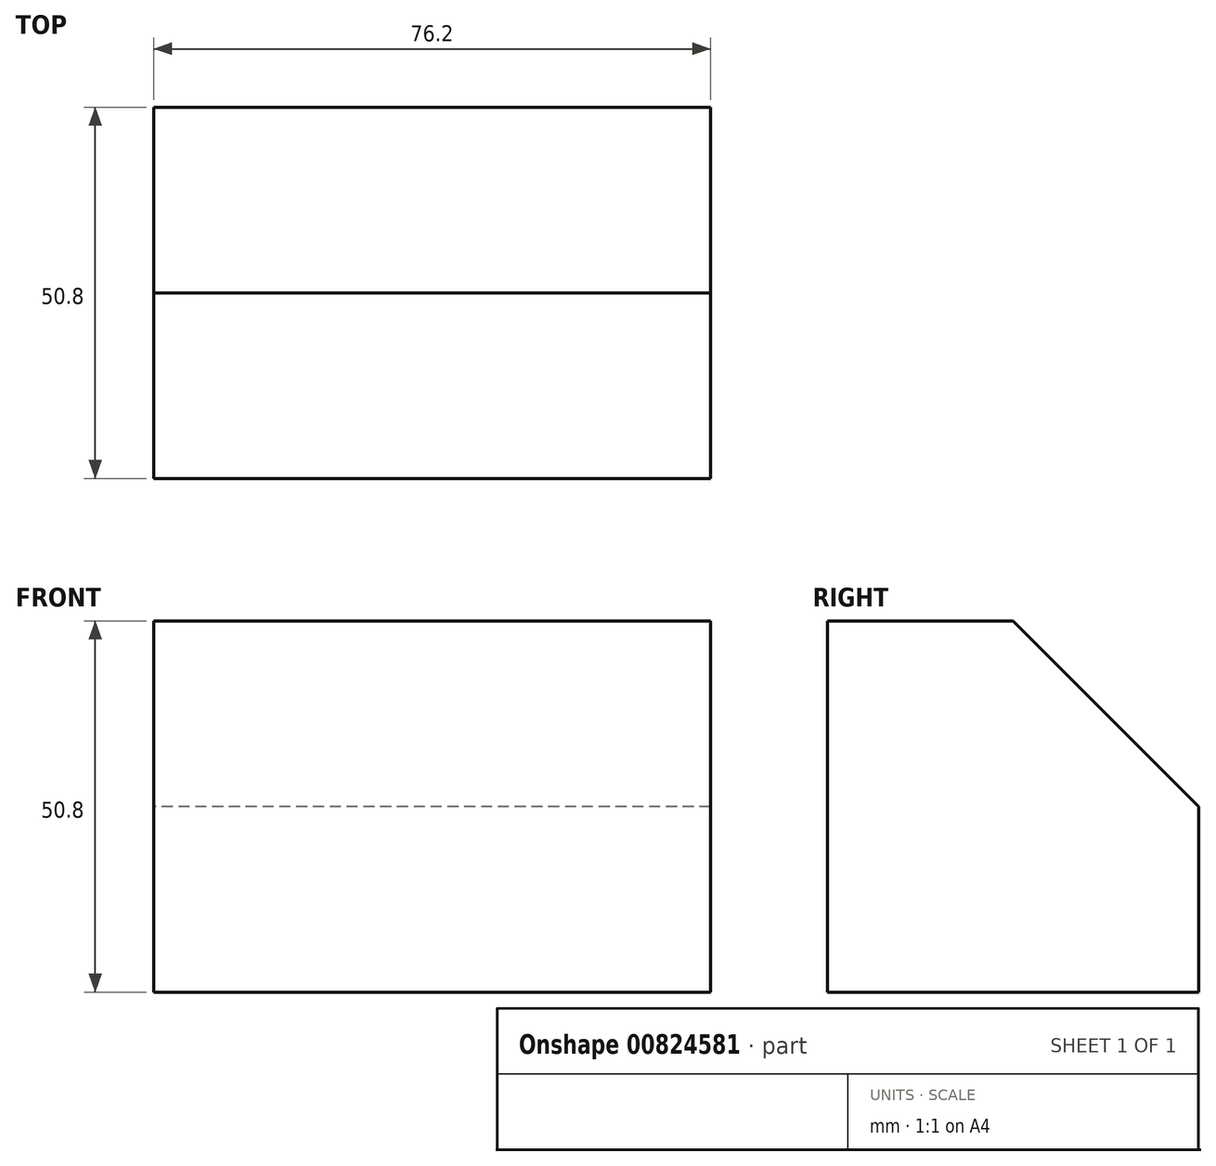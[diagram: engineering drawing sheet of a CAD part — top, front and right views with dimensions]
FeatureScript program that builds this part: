
annotation { "Feature Type Name" : "Feature", "Feature Type Description" : "" }
export const myFeature = defineFeature(function(context is Context, id is Id, definition is map)
    precondition{}
    {
        {
            var Q0;
            Q0=qCreatedBy(makeId("Front.planeOp"),FACE);
            var sketch = newSketch(context, id + "F0", { "sketchPlane" : qUnion([Q0])});
            skLineSegment(sketch, "E0", {"start": v(0, 0) * mm, "end": v(76.2, 0) * mm});
            skLineSegment(sketch, "E1", {"start": v(76.2, 0) * mm, "end": v(76.2, 50.8) * mm});
            skLineSegment(sketch, "E2", {"start": v(76.2, 50.8) * mm, "end": v(0, 50.8) * mm});
            skLineSegment(sketch, "E3", {"start": v(0, 50.8) * mm, "end": v(0, 0) * mm});
            skSolve(sketch);
        }
        {
            var Q0;
            Q0 = qSketchRegion(id + "F0", true);
            extrude(context, id + "F1", {"entities" : qUnion([Q0]), "depth" : 50.8 * mm, "offsetDistance" : 25.4 * mm});
        }
        {
            var Q0;
            Q0=makeQuery(id+"F1.opExtrude","SWEPT_FACE",FACE,{"disambiguationData":[OSD([sQuery(id+"F0.wireOp",EDGE,"E3")])]});
            var sketch = newSketch(context, id + "F2", { "sketchPlane" : qUnion([Q0])});
            skLineSegment(sketch, "E4", {"start": v(0, 0) * mm, "end": v(0, 25.4) * mm});
            skLineSegment(sketch, "E5", {"start": v(0, 25.4) * mm, "end": v(25.4, 50.8) * mm});
            skLineSegment(sketch, "E6", {"start": v(25.4, 50.8) * mm, "end": v(25.4, 0) * mm});
            skLineSegment(sketch, "E7", {"start": v(25.4, 0) * mm, "end": v(25.4, 25.4) * mm});
            skLineSegment(sketch, "E8", {"start": v(25.4, 25.4) * mm, "end": v(0, 25.4) * mm});
            skSolve(sketch);
        }
        {
            var Q0;
            {var subQ0=sQuery(id+"F2.wireOp",EDGE,"E5");Q0=makeQuery(id+"F2.imprint","IMPRINT",FACE,{"disambiguationData":[TD([[makeQuery(id+"F2.imprint","IMPRINT",EDGE,{"derivedFrom":subQ0}),1.0]])]});}
            extrude(context, id + "F3", {"entities" : qUnion([Q0]), "operationType" : NewBodyOperationType.REMOVE, "endBound" : BoundingType.THROUGH_ALL, "oppositeDirection" : true, "depth" : 25.4 * mm, "offsetDistance" : 25.4 * mm});
        }
    });
